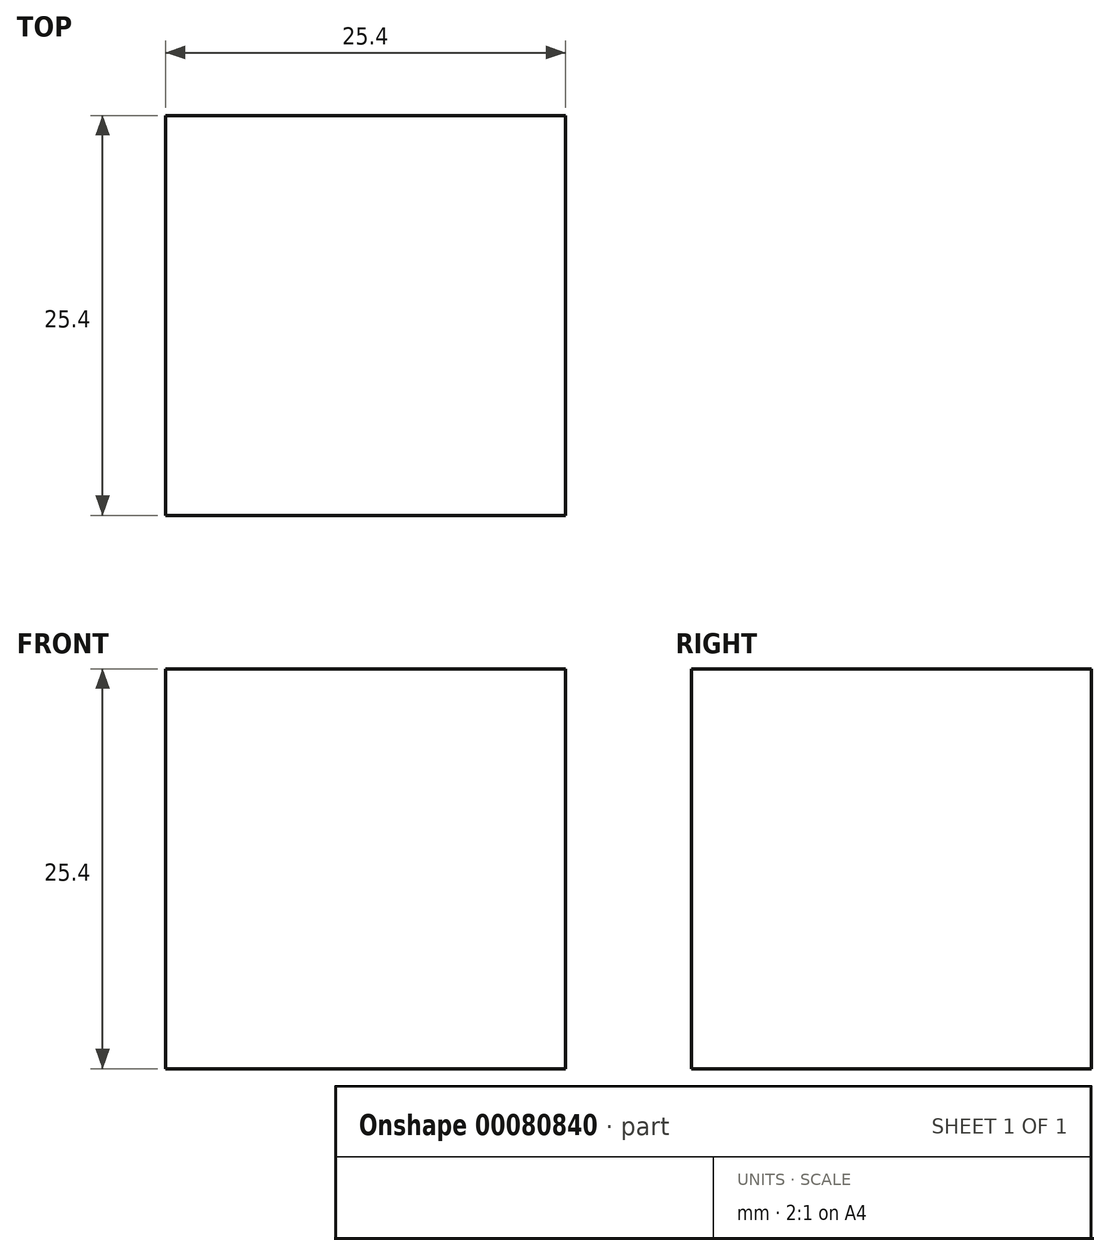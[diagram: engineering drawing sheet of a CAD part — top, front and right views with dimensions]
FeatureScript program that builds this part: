
annotation { "Feature Type Name" : "Feature", "Feature Type Description" : "" }
export const myFeature = defineFeature(function(context is Context, id is Id, definition is map)
    precondition{}
    {
        {
            var Q0;
            Q0=qCreatedBy(makeId("Top.planeOp"),FACE);
            var sketch = newSketch(context, id + "F0", { "sketchPlane" : qUnion([Q0])});
            skLineSegment(sketch, "E0.bottom", {"start": v(-12.7, -12.7) * mm, "end": v(12.7, -12.7) * mm});
            skLineSegment(sketch, "E0.top", {"start": v(-12.7, 12.7) * mm, "end": v(12.7, 12.7) * mm});
            skLineSegment(sketch, "E0.left", {"start": v(-12.7, -12.7) * mm, "end": v(-12.7, 12.7) * mm});
            skLineSegment(sketch, "E0.right", {"start": v(12.7, -12.7) * mm, "end": v(12.7, 12.7) * mm});
            skLineSegment(sketch, "E1", {"start": v(-12.7, 12.7) * mm, "end": v(12.7, -12.7) * mm, "construction": true});
            skSolve(sketch);
        }
        {
            var Q0;
            Q0=makeQuery(id+"F0.imprint","IMPRINT",FACE,{"disambiguationData":[TD([[makeQuery(id+"F0.imprint","IMPRINT",EDGE,{"derivedFrom":sQuery(id+"F0.wireOp",EDGE,"E0.bottom")}),1.0]])]});
            extrude(context, id + "F1", {"entities" : qUnion([Q0]), "depth" : 25.4 * mm});
        }
    });
